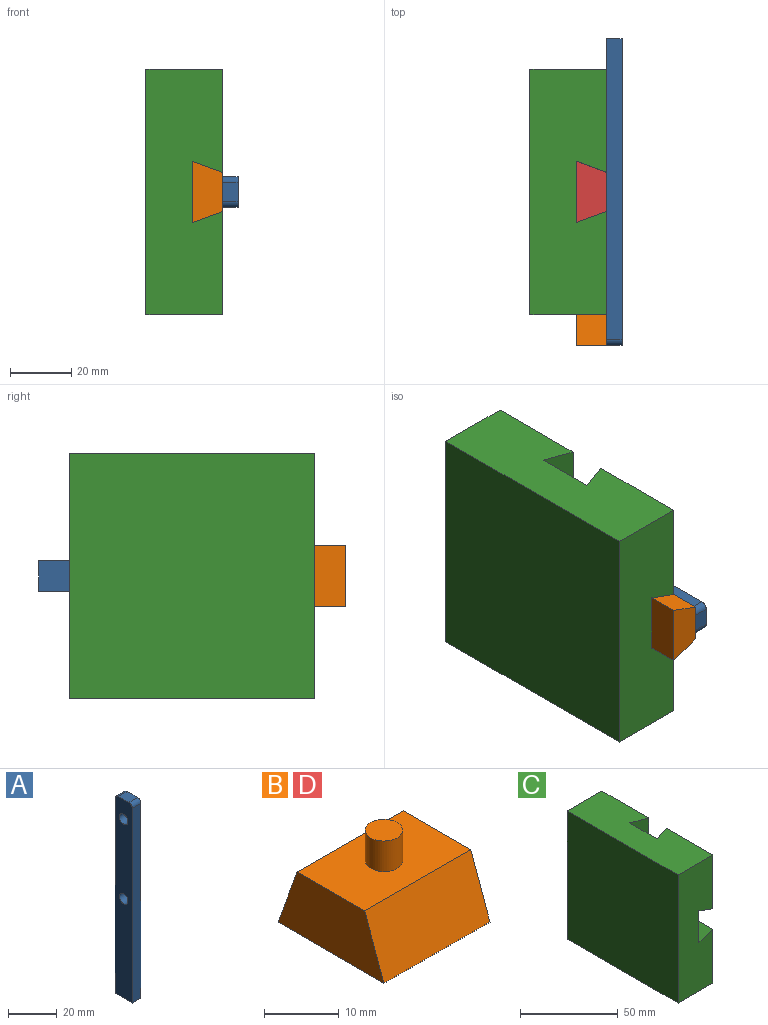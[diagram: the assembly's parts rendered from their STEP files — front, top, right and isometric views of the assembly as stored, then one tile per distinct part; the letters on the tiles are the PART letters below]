
ASSEMBLY  parts=4 mates=4
PART A: 10 faces, bbox 5x10x100 mm
  f0: cylinder r=2mm len=5mm, axis (-1,0,0), area 15.7mm2, adj f1,f7,f8,f9
  f1: plane 6x5mm, normal (0,0,1), area 30mm2, adj f0,f2,f8,f9
  f2: cylinder r=2mm len=5mm, axis (-1,0,0), area 15.7mm2, adj f1,f3,f8,f9
  f3: plane 98x5mm, normal (0,-1,0), area 490mm2, adj f2,f4,f8,f9
  f4: plane 10x5mm, normal (0,0,-1), area 50mm2, adj f3,f7,f8,f9
  f5: cylinder r=2.5mm len=5mm, axis (-1,0,0), area 78.5mm2, adj f8,f9
  f6: cylinder r=2.5mm len=5mm, axis (-1,0,0), area 78.5mm2, adj f8,f9
  f7: plane 98x5mm, normal (0,1,0), area 490mm2, adj f0,f4,f8,f9
  f8: plane 100x10mm, normal (1,0,0), area 959mm2, adj f0,f1,f2,f3,f4,f5,f6,f7
  f9: plane 100x10mm, normal (-1,0,0), area 959mm2, adj f0,f1,f2,f3,f4,f5,f6,f7
PART B: 8 faces, bbox 20x20x15 mm
  f0: plane 20x12.72mm, normal (0,0,1), area 234.8mm2, adj f1,f3,f4,f5,f6
  f1: plane 20x10mm, normal (0,-0.94,0.34), area 212.8mm2, adj f0,f2,f4,f5
  f2: plane 20x20mm, normal (0,0,-1), area 400mm2, adj f1,f3,f4,f5
  f3: plane 20x10mm, normal (0,0.94,0.34), area 212.8mm2, adj f0,f2,f4,f5
  f4: plane 20x10mm, normal (1,0,0), area 163.6mm2, adj f0,f1,f2,f3
  f5: plane 20x10mm, normal (-1,0,0), area 163.6mm2, adj f0,f1,f2,f3
  f6: cylinder r=2.5mm len=5mm, axis (0,0,-1), area 78.5mm2, adj f0,f7
  f7: plane 5x5mm, normal (0,0,1), area 19.6mm2, adj f6
PART C: 18 faces, bbox 25x80x80 mm
  f0: plane 33.64x33.64mm, normal (1,0,0), area 1131.6mm2, adj f2,f4,f8,f14
  f1: plane 33.64x33.64mm, normal (1,0,0), area 1131.6mm2, adj f3,f7,f8,f17
  f2: plane 80x25mm, normal (0,1,0), area 1836.4mm2, adj f0,f5,f6,f8,f10,f12,f14,f15
  f3: plane 33.64x10mm, normal (-0.34,0.94,0), area 338.6mm2, adj f1,f8,f12,f17
  f4: plane 33.64x10mm, normal (-0.34,-0.94,0), area 338.6mm2, adj f0,f8,f12,f14
  f5: plane 33.64x33.64mm, normal (1,0,0), area 1131.6mm2, adj f2,f6,f13,f15
  f6: plane 80x25mm, normal (0,0,1), area 1836.4mm2, adj f2,f5,f7,f9,f10,f11,f12,f13
  f7: plane 80x25mm, normal (0,-1,0), area 1836.4mm2, adj f1,f6,f8,f9,f10,f12,f16,f17
  f8: plane 80x25mm, normal (0,0,-1), area 1836.4mm2, adj f0,f1,f2,f3,f4,f7,f10,f12
  f9: plane 33.64x33.64mm, normal (1,0,0), area 1131.6mm2, adj f6,f7,f11,f16
  f10: plane 80x80mm, normal (-1,0,0), area 6400mm2, adj f2,f6,f7,f8
  f11: plane 33.64x10mm, normal (-0.34,0.94,0), area 338.6mm2, adj f6,f9,f12,f16
  f12: plane 80x80mm, normal (1,0,0), area 2800mm2, adj f2,f3,f4,f6,f7,f8,f11,f13
  f13: plane 33.64x10mm, normal (-0.34,-0.94,0), area 338.6mm2, adj f5,f6,f12,f15
  f14: plane 33.64x10mm, normal (-0.34,0,0.94), area 338.6mm2, adj f0,f2,f4,f12
  f15: plane 33.64x10mm, normal (-0.34,0,-0.94), area 338.6mm2, adj f2,f5,f12,f13
  f16: plane 33.64x10mm, normal (-0.34,0,-0.94), area 338.6mm2, adj f7,f9,f11,f12
  f17: plane 33.64x10mm, normal (-0.34,0,0.94), area 338.6mm2, adj f1,f3,f7,f12
PART D: same geometry as B
PLACE A rot(axis=(1,0,0),90deg) t=(15.63,38.2,32.59)mm
PLACE B rot(axis=(0.58,0.58,0.58),120deg) t=(10.63,-64.66,-3.42)mm
PLACE C rot(axis=(0.98,0.13,0.17),0deg) t=(-9.37,25.34,-43.42)mm
PLACE D rot(axis=(0,1,0),90deg) t=(10.63,-14.66,6.58)mm
MATE slider B.f5 <-> C.f7  axis (0,-1,0) through (5.63,-64.66,-3.42)mm
MATE slider C.f8 <-> D.f4  axis (0,0,-1) through (5.63,-14.66,-43.42)mm
MATE revolute A.f6 <-> D.f6  axis (1,0,0) through (20.63,-14.66,-3.42)mm
MATE revolute B.f6 <-> A.f5  axis (1,0,0) through (20.63,-54.66,-3.42)mm
